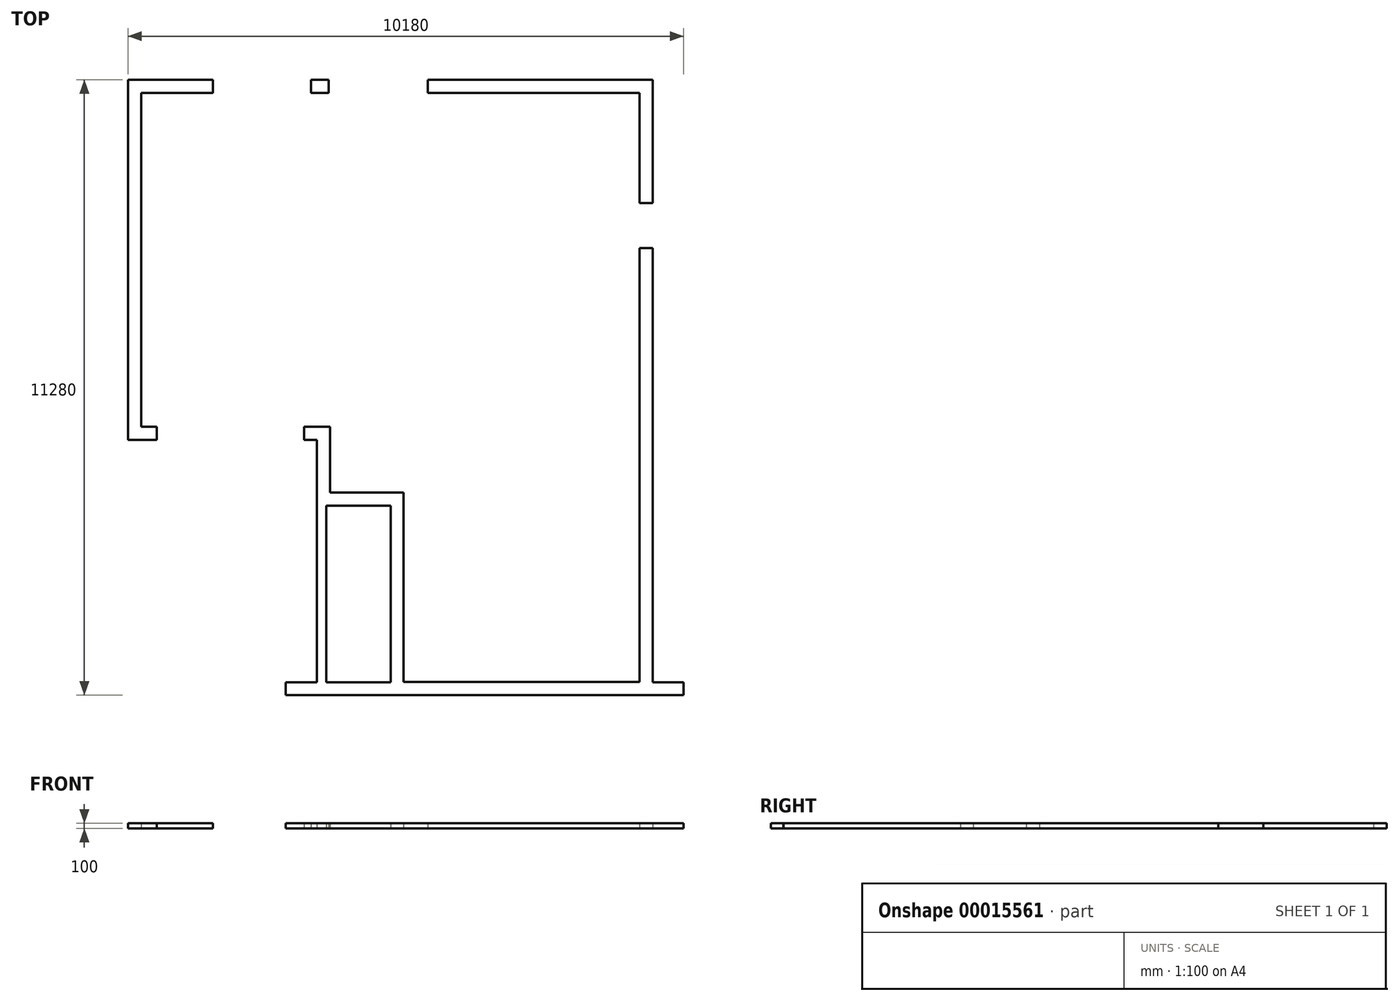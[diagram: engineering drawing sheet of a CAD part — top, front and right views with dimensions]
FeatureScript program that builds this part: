
annotation { "Feature Type Name" : "Feature", "Feature Type Description" : "" }
export const myFeature = defineFeature(function(context is Context, id is Id, definition is map)
    precondition{}
    {
        {
            var Q0;
            Q0=qCreatedBy(makeId("Top.planeOp"),FACE);
            var sketch = newSketch(context, id + "F0", { "sketchPlane" : qUnion([Q0])});
            skLineSegment(sketch, "E0", {"start": v(0, 0) * mm, "end": v(9610, 0) * mm});
            skLineSegment(sketch, "E1", {"start": v(9610, 0) * mm, "end": v(9610, -11280) * mm});
            skLineSegment(sketch, "E2", {"start": v(9610, -11280) * mm, "end": v(4810, -11280) * mm});
            skLineSegment(sketch, "E3", {"start": v(3460, -11280) * mm, "end": v(3460, -6600) * mm});
            skLineSegment(sketch, "E4", {"start": v(3460, -6600) * mm, "end": v(0, -6600) * mm});
            skLineSegment(sketch, "E5", {"start": v(0, -6600) * mm, "end": v(0, 0) * mm});
            skLineSegment(sketch, "E6", {"start": v(3460, -6600) * mm, "end": v(3700, -6600) * mm});
            skLineSegment(sketch, "E7", {"start": v(4810, -7570) * mm, "end": v(4810, -11280) * mm});
            skLineSegment(sketch, "E8.0", {"start": v(9370, -11040) * mm, "end": v(5050, -11040) * mm});
            skLineSegment(sketch, "E8.1", {"start": v(9370, -240) * mm, "end": v(9370, -11040) * mm});
            skLineSegment(sketch, "E8.3", {"start": v(3700, -6360) * mm, "end": v(240, -6360) * mm});
            skLineSegment(sketch, "E8.4", {"start": v(240, -6360) * mm, "end": v(240, -240) * mm});
            skLineSegment(sketch, "E8.5", {"start": v(240, -240) * mm, "end": v(9370, -240) * mm});
            skLineSegment(sketch, "E9", {"start": v(4810, -11280) * mm, "end": v(3460, -11280) * mm});
            skLineSegment(sketch, "E10.0", {"start": v(5050, -7570) * mm, "end": v(5050, -11040) * mm});
            skLineSegment(sketch, "E11.bottom", {"start": v(1555, 0) * mm, "end": v(3350, 0) * mm});
            skLineSegment(sketch, "E11.top", {"start": v(1555, -240) * mm, "end": v(3350, -240) * mm});
            skLineSegment(sketch, "E11.left", {"start": v(1555, 0) * mm, "end": v(1555, -240) * mm});
            skLineSegment(sketch, "E11.right", {"start": v(3350, 0) * mm, "end": v(3350, -240) * mm});
            skLineSegment(sketch, "E12.bottom", {"start": v(5490, 0) * mm, "end": v(3675, 0) * mm});
            skLineSegment(sketch, "E12.top", {"start": v(5490, -240) * mm, "end": v(3675, -240) * mm});
            skLineSegment(sketch, "E12.left", {"start": v(5490, 0) * mm, "end": v(5490, -240) * mm});
            skLineSegment(sketch, "E12.right", {"start": v(3675, 0) * mm, "end": v(3675, -240) * mm});
            skLineSegment(sketch, "E13.bottom", {"start": v(5970, -240) * mm, "end": v(6070, -240) * mm});
            skLineSegment(sketch, "E13.top", {"start": v(5970, -2940) * mm, "end": v(6070, -2940) * mm});
            skLineSegment(sketch, "E13.left", {"start": v(5970, -240) * mm, "end": v(5970, -2940) * mm});
            skLineSegment(sketch, "E13.right", {"start": v(6070, -240) * mm, "end": v(6070, -2940) * mm});
            skLineSegment(sketch, "E14.bottom", {"start": v(6070, -2940) * mm, "end": v(9370, -2940) * mm});
            skLineSegment(sketch, "E14.top", {"start": v(6070, -2840) * mm, "end": v(9370, -2840) * mm});
            skLineSegment(sketch, "E14.left", {"start": v(6070, -2940) * mm, "end": v(6070, -2840) * mm});
            skLineSegment(sketch, "E14.right", {"start": v(9370, -2940) * mm, "end": v(9370, -2840) * mm});
            skLineSegment(sketch, "E15", {"start": v(9370, -820) * mm, "end": v(9610, -820) * mm});
            skLineSegment(sketch, "E16", {"start": v(9370, -2260) * mm, "end": v(9610, -2260) * mm});
            skLineSegment(sketch, "E17", {"start": v(9370, -3085) * mm, "end": v(9610, -3085) * mm});
            skLineSegment(sketch, "E18", {"start": v(9370, -4525) * mm, "end": v(9610, -4525) * mm});
            skLineSegment(sketch, "E19", {"start": v(9610, -11050) * mm, "end": v(9370, -11050) * mm});
            skLineSegment(sketch, "E20", {"start": v(9370, -5470) * mm, "end": v(9610, -5470) * mm});
            skLineSegment(sketch, "E21", {"start": v(9370, -6910) * mm, "end": v(9610, -6910) * mm});
            skLineSegment(sketch, "E22", {"start": v(3700, -6360) * mm, "end": v(3700, -6600) * mm});
            skLineSegment(sketch, "E23", {"start": v(3700, -7570) * mm, "end": v(4810, -7570) * mm});
            skLineSegment(sketch, "E24", {"start": v(5050, -7570) * mm, "end": v(5050, -7810) * mm});
            skLineSegment(sketch, "E25", {"start": v(4810, -7810) * mm, "end": v(3460, -7810) * mm});
            skLineSegment(sketch, "E26", {"start": v(3930, -7570) * mm, "end": v(3930, -7810) * mm});
            skLineSegment(sketch, "E27.bottom", {"start": v(4810, -11280) * mm, "end": v(4690, -11280) * mm});
            skLineSegment(sketch, "E27.top", {"start": v(4810, -11050) * mm, "end": v(4690, -11050) * mm});
            skLineSegment(sketch, "E27.left", {"start": v(4810, -11280) * mm, "end": v(4810, -11050) * mm});
            skLineSegment(sketch, "E27.right", {"start": v(4690, -11280) * mm, "end": v(4690, -11050) * mm});
            skLineSegment(sketch, "E28", {"start": v(3700, -6600) * mm, "end": v(3700, -7570) * mm});
            skLineSegment(sketch, "E29", {"start": v(4810, -7570) * mm, "end": v(5050, -7570) * mm});
            skLineSegment(sketch, "E30.bottom", {"start": v(9370, -4790) * mm, "end": v(5970, -4790) * mm});
            skLineSegment(sketch, "E30.top", {"start": v(9370, -4890) * mm, "end": v(5970, -4890) * mm});
            skLineSegment(sketch, "E30.left", {"start": v(9370, -4790) * mm, "end": v(9370, -4890) * mm});
            skLineSegment(sketch, "E30.right", {"start": v(5970, -4790) * mm, "end": v(5970, -4890) * mm});
            skLineSegment(sketch, "E31.bottom", {"start": v(5970, -4790) * mm, "end": v(6070, -4790) * mm});
            skLineSegment(sketch, "E31.top", {"start": v(5970, -3790) * mm, "end": v(6070, -3790) * mm});
            skLineSegment(sketch, "E31.left", {"start": v(5970, -4790) * mm, "end": v(5970, -3790) * mm});
            skLineSegment(sketch, "E31.right", {"start": v(6070, -4790) * mm, "end": v(6070, -3790) * mm});
            skLineSegment(sketch, "E32.bottom", {"start": v(6070, -3790) * mm, "end": v(7080, -3790) * mm});
            skLineSegment(sketch, "E32.top", {"start": v(6070, -3890) * mm, "end": v(7080, -3890) * mm});
            skLineSegment(sketch, "E32.left", {"start": v(6070, -3790) * mm, "end": v(6070, -3890) * mm});
            skLineSegment(sketch, "E32.right", {"start": v(7080, -3790) * mm, "end": v(7080, -3890) * mm});
            skLineSegment(sketch, "E33.bottom", {"start": v(7080, -3790) * mm, "end": v(6980, -3790) * mm});
            skLineSegment(sketch, "E33.top", {"start": v(7080, -2940) * mm, "end": v(6980, -2940) * mm});
            skLineSegment(sketch, "E33.left", {"start": v(7080, -3790) * mm, "end": v(7080, -2940) * mm});
            skLineSegment(sketch, "E33.right", {"start": v(6980, -3790) * mm, "end": v(6980, -2940) * mm});
            skLineSegment(sketch, "E34.bottom", {"start": v(5970, -4890) * mm, "end": v(6070, -4890) * mm});
            skLineSegment(sketch, "E34.top", {"start": v(5970, -7570) * mm, "end": v(6070, -7570) * mm});
            skLineSegment(sketch, "E34.left", {"start": v(5970, -4890) * mm, "end": v(5970, -7570) * mm});
            skLineSegment(sketch, "E34.right", {"start": v(6070, -4890) * mm, "end": v(6070, -7570) * mm});
            skLineSegment(sketch, "E35.bottom", {"start": v(5932.46, -7570) * mm, "end": v(9370, -7570) * mm});
            skLineSegment(sketch, "E35.top", {"start": v(5932.46, -7670) * mm, "end": v(9370, -7670) * mm});
            skLineSegment(sketch, "E35.left", {"start": v(5932.46, -7570) * mm, "end": v(5932.46, -7670) * mm});
            skLineSegment(sketch, "E35.right", {"start": v(9370, -7570) * mm, "end": v(9370, -7670) * mm});
            skLineSegment(sketch, "E36.bottom", {"start": v(5050, -7570) * mm, "end": v(5932.46, -7570) * mm});
            skLineSegment(sketch, "E36.top", {"start": v(5050, -7670) * mm, "end": v(5932.46, -7670) * mm});
            skLineSegment(sketch, "E36.left", {"start": v(5050, -7570) * mm, "end": v(5050, -7670) * mm});
            skLineSegment(sketch, "E37.bottom", {"start": v(5932.46, -7570) * mm, "end": v(5092.46, -7570) * mm});
            skLineSegment(sketch, "E37.top", {"start": v(5932.46, -7670) * mm, "end": v(5092.46, -7670) * mm});
            skLineSegment(sketch, "E37.right", {"start": v(5092.46, -7570) * mm, "end": v(5092.46, -7670) * mm});
            skLineSegment(sketch, "E38.bottom", {"start": v(240, -2840) * mm, "end": v(3910, -2840) * mm});
            skLineSegment(sketch, "E38.top", {"start": v(240, -2940) * mm, "end": v(3910, -2940) * mm});
            skLineSegment(sketch, "E38.left", {"start": v(240, -2840) * mm, "end": v(240, -2940) * mm});
            skLineSegment(sketch, "E38.right", {"start": v(3910, -2840) * mm, "end": v(3910, -2940) * mm});
            skLineSegment(sketch, "E39.bottom", {"start": v(3700, -6360) * mm, "end": v(5050, -6360) * mm});
            skLineSegment(sketch, "E39.top", {"start": v(3700, -6460) * mm, "end": v(5050, -6460) * mm});
            skLineSegment(sketch, "E39.left", {"start": v(3700, -6360) * mm, "end": v(3700, -6460) * mm});
            skLineSegment(sketch, "E39.right", {"start": v(5050, -6360) * mm, "end": v(5050, -6460) * mm});
            skLineSegment(sketch, "E40.bottom", {"start": v(5050, -6360) * mm, "end": v(4390, -6360) * mm});
            skLineSegment(sketch, "E40.top", {"start": v(5050, -4020) * mm, "end": v(4390, -4020) * mm});
            skLineSegment(sketch, "E40.left", {"start": v(5050, -6360) * mm, "end": v(5050, -4020) * mm});
            skLineSegment(sketch, "E40.right", {"start": v(4390, -6360) * mm, "end": v(4390, -4020) * mm});
            skLineSegment(sketch, "E41.bottom", {"start": v(3630, -11280) * mm, "end": v(2890, -11280) * mm});
            skLineSegment(sketch, "E41.top", {"start": v(3630, -11050) * mm, "end": v(2890, -11050) * mm});
            skLineSegment(sketch, "E41.left", {"start": v(3630, -11280) * mm, "end": v(3630, -11050) * mm});
            skLineSegment(sketch, "E41.right", {"start": v(2890, -11280) * mm, "end": v(2890, -11050) * mm});
            skLineSegment(sketch, "E42.bottom", {"start": v(9610, -11280) * mm, "end": v(10180, -11280) * mm});
            skLineSegment(sketch, "E42.top", {"start": v(9610, -11050) * mm, "end": v(10180, -11050) * mm});
            skLineSegment(sketch, "E42.left", {"start": v(9610, -11280) * mm, "end": v(9610, -11050) * mm});
            skLineSegment(sketch, "E42.right", {"start": v(10180, -11280) * mm, "end": v(10180, -11050) * mm});
            skLineSegment(sketch, "E43.bottom", {"start": v(525, -6360) * mm, "end": v(3225, -6360) * mm});
            skLineSegment(sketch, "E43.top", {"start": v(525, -6600) * mm, "end": v(3225, -6600) * mm});
            skLineSegment(sketch, "E43.left", {"start": v(525, -6360) * mm, "end": v(525, -6600) * mm});
            skLineSegment(sketch, "E43.right", {"start": v(3225, -6360) * mm, "end": v(3225, -6600) * mm});
            skLineSegment(sketch, "E44", {"start": v(3630, -11050) * mm, "end": v(4690, -11050) * mm});
            skLineSegment(sketch, "E45", {"start": v(3630, -11050) * mm, "end": v(3630, -7810) * mm});
            skSolve(sketch);
        }
        {
            var Q0;
            Q0=qCreatedBy(makeId("Top.planeOp"),FACE);
            var sketch = newSketch(context, id + "F1", { "sketchPlane" : qUnion([Q0])});
            skLineSegment(sketch, "E46", {"start": v(9305, -7900) * mm, "end": v(305, -7900) * mm, "construction": true});
            skLineSegment(sketch, "E47", {"start": v(9305, 200) * mm, "end": v(305, 200) * mm, "construction": true});
            skLineSegment(sketch, "E48", {"start": v(305, 3950) * mm, "end": v(9305, 3950) * mm, "construction": true});
            skLineSegment(sketch, "E49", {"start": v(100, -7900) * mm, "end": v(100, 3950) * mm, "construction": true});
            skLineSegment(sketch, "E50", {"start": v(9510, 3950) * mm, "end": v(9510, -7900) * mm, "construction": true});
            skLineSegment(sketch, "E51", {"start": v(6310, -7900) * mm, "end": v(6310, 3950) * mm, "construction": true});
            skLineSegment(sketch, "E52", {"start": v(3300, 3950) * mm, "end": v(3300, -7900) * mm, "construction": true});
            skLineSegment(sketch, "E53", {"start": v(3300, 3450) * mm, "end": v(6310, 3450) * mm, "construction": true});
            skLineSegment(sketch, "E54", {"start": v(4805, 3450) * mm, "end": v(4805, 3950) * mm, "construction": true});
            skSolve(sketch);
        }
        {
            var Q0;
            {var subQ0=sQuery(id+"F0.wireOp",EDGE,"E5");Q0=makeQuery(id+"F0.imprint","IMPRINT",FACE,{"disambiguationData":[TD([[makeQuery(id+"F0.imprint","IMPRINT",EDGE,{"derivedFrom":subQ0}),-1.0]])]});}
            var Q1;
            Q1=makeQuery(id+"F0.imprint","IMPRINT",FACE,{"disambiguationData":[TD([[makeQuery(id+"F0.imprint","IMPRINT",EDGE,{"derivedFrom":sQuery(id+"F0.wireOp",EDGE,"E43.bottom")}),-1.0]])]});
            var Q2;
            Q2=makeQuery(id+"F0.imprint","IMPRINT",FACE,{"disambiguationData":[TD([[makeQuery(id+"F0.imprint","IMPRINT",EDGE,{"derivedFrom":sQuery(id+"F0.wireOp",EDGE,"E11.bottom")}),-1.0]])]});
            var Q3;
            {var subQ0=sQuery(id+"F0.wireOp",EDGE,"E11.right");Q3=makeQuery(id+"F0.imprint","IMPRINT",FACE,{"disambiguationData":[TD([[makeQuery(id+"F0.imprint","IMPRINT",EDGE,{"derivedFrom":subQ0}),1.0]])]});}
            var Q4;
            Q4=makeQuery(id+"F0.imprint","IMPRINT",FACE,{"disambiguationData":[TD([[makeQuery(id+"F0.imprint","IMPRINT",EDGE,{"derivedFrom":sQuery(id+"F0.wireOp",EDGE,"E12.bottom")}),1.0]])]});
            var Q5;
            {var subQ0=sQuery(id+"F0.wireOp",EDGE,"E12.left");Q5=makeQuery(id+"F0.imprint","IMPRINT",FACE,{"disambiguationData":[TD([[makeQuery(id+"F0.imprint","IMPRINT",EDGE,{"derivedFrom":subQ0}),1.0]])]});}
            var Q6;
            {var subQ0=sQuery(id+"F0.wireOp",EDGE,"E15");Q6=makeQuery(id+"F0.imprint","IMPRINT",FACE,{"disambiguationData":[TD([[makeQuery(id+"F0.imprint","IMPRINT",EDGE,{"derivedFrom":subQ0}),-1.0]])]});}
            var Q7;
            {var subQ0=sQuery(id+"F0.wireOp",EDGE,"E14.right");Q7=makeQuery(id+"F0.imprint","IMPRINT",FACE,{"disambiguationData":[TD([[makeQuery(id+"F0.imprint","IMPRINT",EDGE,{"derivedFrom":subQ0}),-1.0]])]});}
            var Q8;
            {var subQ0=sQuery(id+"F0.wireOp",EDGE,"E17");Q8=makeQuery(id+"F0.imprint","IMPRINT",FACE,{"disambiguationData":[TD([[makeQuery(id+"F0.imprint","IMPRINT",EDGE,{"derivedFrom":subQ0}),-1.0]])]});}
            var Q9;
            {var subQ0=sQuery(id+"F0.wireOp",EDGE,"E18");Q9=makeQuery(id+"F0.imprint","IMPRINT",FACE,{"disambiguationData":[TD([[makeQuery(id+"F0.imprint","IMPRINT",EDGE,{"derivedFrom":subQ0}),-1.0]])]});}
            var Q10;
            {var subQ0=sQuery(id+"F0.wireOp",EDGE,"E20");Q10=makeQuery(id+"F0.imprint","IMPRINT",FACE,{"disambiguationData":[TD([[makeQuery(id+"F0.imprint","IMPRINT",EDGE,{"derivedFrom":subQ0}),-1.0]])]});}
            var Q11;
            Q11=makeQuery(id+"F0.imprint","IMPRINT",FACE,{"disambiguationData":[TD([[makeQuery(id+"F0.imprint","IMPRINT",EDGE,{"derivedFrom":sQuery(id+"F0.wireOp",EDGE,"E2")}),-1.0]])]});
            var Q12;
            {var subQ3=sQuery(id+"F0.wireOp",EDGE,"E6");Q12=makeQuery(id+"F0.imprint","IMPRINT",FACE,{"disambiguationData":[TD([[makeQuery(id+"F0.imprint","IMPRINT",EDGE,{"derivedFrom":subQ3}),1.0]])]});}
            var Q13;
            {var subQ6=sQuery(id+"F0.wireOp",EDGE,"E6");Q13=makeQuery(id+"F0.imprint","IMPRINT",FACE,{"disambiguationData":[TD([[makeQuery(id+"F0.imprint","IMPRINT",EDGE,{"derivedFrom":subQ6}),-1.0]])]});}
            var Q14;
            {var subQ5=sQuery(id+"F0.wireOp",EDGE,"E26");Q14=makeQuery(id+"F0.imprint","IMPRINT",FACE,{"disambiguationData":[TD([[makeQuery(id+"F0.imprint","IMPRINT",EDGE,{"derivedFrom":subQ5}),1.0]])]});}
            var Q15;
            {var subQ5=sQuery(id+"F0.wireOp",EDGE,"E41.right");Q15=makeQuery(id+"F0.imprint","IMPRINT",FACE,{"disambiguationData":[TD([[makeQuery(id+"F0.imprint","IMPRINT",EDGE,{"derivedFrom":subQ5}),-1.0]])]});}
            var Q16;
            {var subQ5=sQuery(id+"F0.wireOp",EDGE,"E41.left");Q16=makeQuery(id+"F0.imprint","IMPRINT",FACE,{"disambiguationData":[TD([[makeQuery(id+"F0.imprint","IMPRINT",EDGE,{"derivedFrom":subQ5}),1.0]])]});}
            var Q17;
            Q17=makeQuery(id+"F0.imprint","IMPRINT",FACE,{"disambiguationData":[TD([[makeQuery(id+"F0.imprint","IMPRINT",EDGE,{"derivedFrom":sQuery(id+"F0.wireOp",EDGE,"E27.bottom")}),-1.0]])]});
            var Q18;
            Q18=makeQuery(id+"F0.imprint","IMPRINT",FACE,{"disambiguationData":[TD([[makeQuery(id+"F0.imprint","IMPRINT",EDGE,{"derivedFrom":sQuery(id+"F0.wireOp",EDGE,"E42.bottom")}),1.0]])]});
            var Q19;
            {var subQ5=sQuery(id+"F0.wireOp",EDGE,"E45");Q19=makeQuery(id+"F0.imprint","IMPRINT",FACE,{"disambiguationData":[TD([[makeQuery(id+"F0.imprint","IMPRINT",EDGE,{"derivedFrom":subQ5}),1.0]])]});}
            var Q20;
            Q20=makeQuery(id+"F0.imprint","IMPRINT",FACE,{"disambiguationData":[TD([[makeQuery(id+"F0.imprint","IMPRINT",EDGE,{"derivedFrom":sQuery(id+"F0.wireOp",EDGE,"E9")}),-1.0]])]});
            extrude(context, id + "F2", {"entities" : qUnion([Q0, Q1, Q2, Q3, Q4, Q5, Q6, Q7, Q8, Q9, Q10, Q11, Q12, Q13, Q14, Q15, Q16, Q17, Q18, Q19, Q20]), "depth" : 100 * mm});
        }
    });
